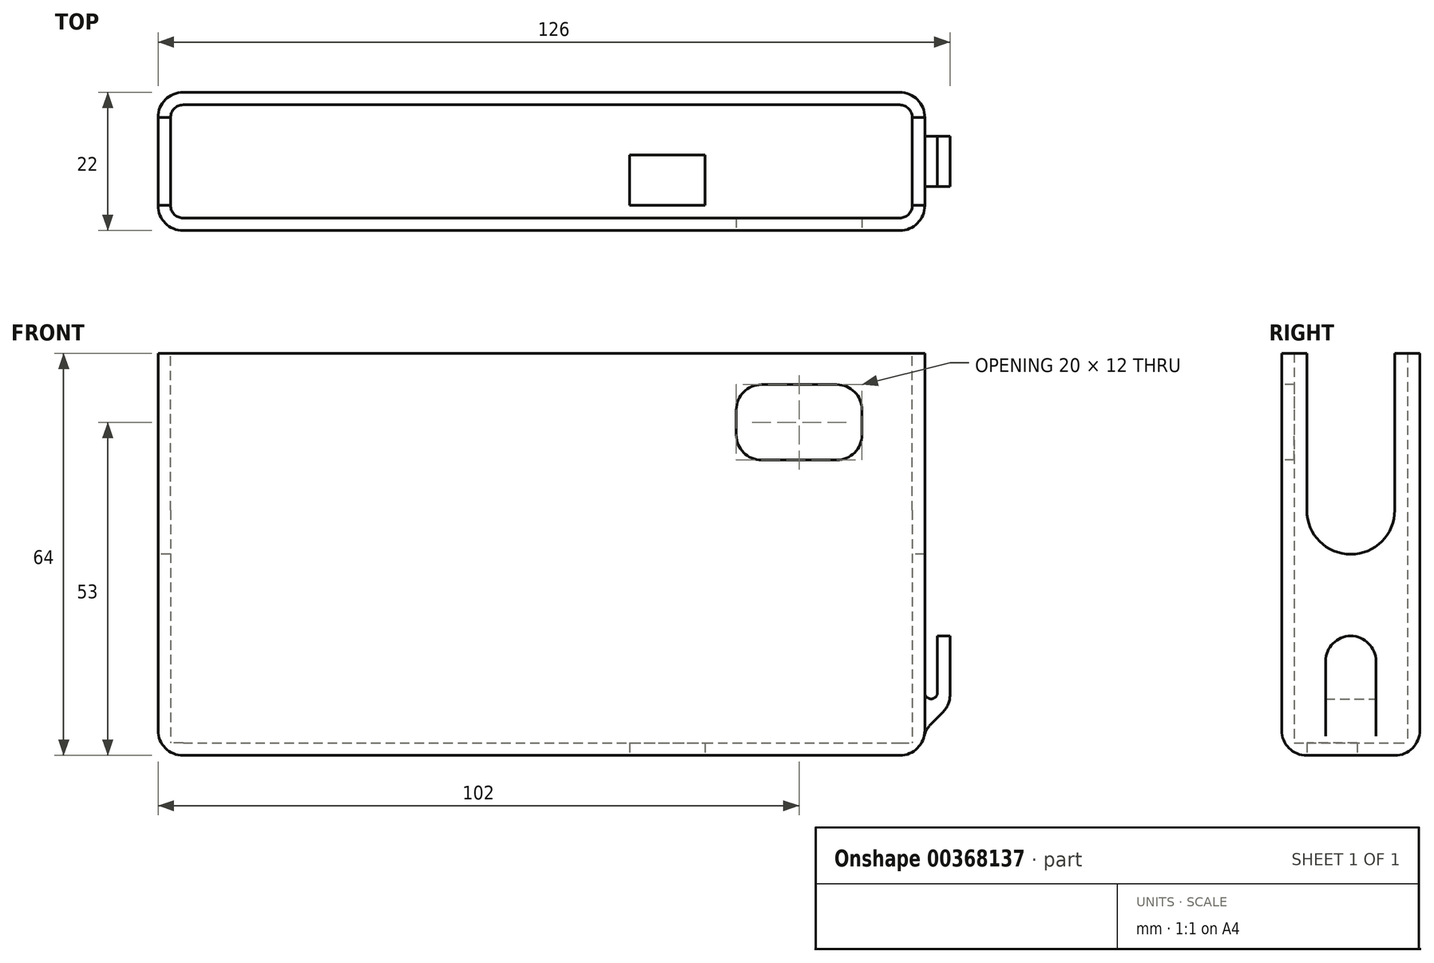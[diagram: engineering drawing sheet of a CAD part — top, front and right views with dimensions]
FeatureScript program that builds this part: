
annotation { "Feature Type Name" : "Feature", "Feature Type Description" : "" }
export const myFeature = defineFeature(function(context is Context, id is Id, definition is map)
    precondition{}
    {
        {
            var Q0;
            Q0=qCreatedBy(makeId("Top.planeOp"),FACE);
            var sketch = newSketch(context, id + "F0", { "sketchPlane" : qUnion([Q0])});
            skLineSegment(sketch, "E0.bottom", {"start": v(0, 0) * mm, "end": v(122, 0) * mm});
            skLineSegment(sketch, "E0.top", {"start": v(0, 22) * mm, "end": v(122, 22) * mm});
            skLineSegment(sketch, "E0.left", {"start": v(0, 0) * mm, "end": v(0, 22) * mm});
            skLineSegment(sketch, "E0.right", {"start": v(122, 0) * mm, "end": v(122, 22) * mm});
            skSolve(sketch);
        }
        {
            var Q0;
            Q0 = qSketchRegion(id + "F0", true);
            extrude(context, id + "F1", {"entities" : qUnion([Q0]), "depth" : 2 * mm});
        }
        {
            var Q0;
            Q0=makeQuery(id+"F1.opExtrude","CAP_FACE",FACE,{"disambiguationData":[OSD([sQuery(id+"F0.wireOp",EDGE,"E0.bottom"),sQuery(id+"F0.wireOp",EDGE,"E0.top"),sQuery(id+"F0.wireOp",EDGE,"E0.left"),sQuery(id+"F0.wireOp",EDGE,"E0.right")])],"isStart":false});
            var sketch = newSketch(context, id + "F2", { "sketchPlane" : qUnion([Q0])});
            skLineSegment(sketch, "E1.0", {"start": v(0, 22) * mm, "end": v(122, 22) * mm});
            skLineSegment(sketch, "E1.1", {"start": v(0, 0) * mm, "end": v(0, 22) * mm});
            skLineSegment(sketch, "E1.2", {"start": v(0, 0) * mm, "end": v(122, 0) * mm});
            skLineSegment(sketch, "E1.3", {"start": v(122, 0) * mm, "end": v(122, 22) * mm});
            skLineSegment(sketch, "E2.0", {"start": v(2, 20) * mm, "end": v(120, 20) * mm});
            skLineSegment(sketch, "E2.1", {"start": v(2, 2) * mm, "end": v(2, 20) * mm});
            skLineSegment(sketch, "E2.2", {"start": v(2, 2) * mm, "end": v(120, 2) * mm});
            skLineSegment(sketch, "E2.3", {"start": v(120, 2) * mm, "end": v(120, 20) * mm});
            skSolve(sketch);
        }
        {
            var Q0;
            Q0 = qSketchRegion(id + "F2", true);
            extrude(context, id + "F3", {"entities" : qUnion([Q0]), "operationType" : NewBodyOperationType.ADD, "depth" : 62 * mm});
        }
        {
            var Q0;
            Q0=makeQuery(id+"F3.opExtrude","SWEPT_EDGE",EDGE,{"disambiguationData":[OSD([sQuery(id+"F2.wireOp",EDGE,"E2.1"),sQuery(id+"F2.wireOp",EDGE,"E2.2")])]});
            var Q1;
            Q1=makeQuery(id+"F3.opExtrude","SWEPT_EDGE",EDGE,{"disambiguationData":[OSD([sQuery(id+"F2.wireOp",EDGE,"E2.0"),sQuery(id+"F2.wireOp",EDGE,"E2.1")])]});
            var Q2;
            Q2=makeQuery(id+"F3.opExtrude","SWEPT_EDGE",EDGE,{"disambiguationData":[OSD([sQuery(id+"F2.wireOp",EDGE,"E2.0"),sQuery(id+"F2.wireOp",EDGE,"E2.3")])]});
            var Q3;
            Q3=makeQuery(id+"F3.opExtrude","SWEPT_EDGE",EDGE,{"disambiguationData":[OSD([sQuery(id+"F2.wireOp",EDGE,"E2.2"),sQuery(id+"F2.wireOp",EDGE,"E2.3")])]});
            var Q4;
            Q4=makeQuery(id+"F3.opExtrude","CAP_EDGE",EDGE,{"disambiguationData":[OSD([sQuery(id+"F2.wireOp",EDGE,"E2.2")])],"isStart":true});
            var Q5;
            Q5=makeQuery(id+"F3.opExtrude","CAP_EDGE",EDGE,{"disambiguationData":[OSD([sQuery(id+"F2.wireOp",EDGE,"E2.3")])],"isStart":true});
            var Q6;
            Q6=makeQuery(id+"F3.opExtrude","CAP_EDGE",EDGE,{"disambiguationData":[OSD([sQuery(id+"F2.wireOp",EDGE,"E2.0")])],"isStart":true});
            var Q7;
            Q7=makeQuery(id+"F3.opExtrude","CAP_EDGE",EDGE,{"disambiguationData":[OSD([sQuery(id+"F2.wireOp",EDGE,"E2.1")])],"isStart":true});
            fillet(context, id + "F4", {"entities" : qUnion([Q0, Q1, Q2, Q3, Q4, Q5, Q6, Q7]), "radius" : 2 * mm, "tangentPropagation" : true, "allowEdgeOverflow" : false});
        }
        {
            var Q0;
            Q0=makeQuery(id+"F3.boolean.opBoolean","MERGE",EDGE,{"derivedFrom":[makeQuery(id+"F1.opExtrude","SWEPT_EDGE",EDGE,{"disambiguationData":[OSD([sQuery(id+"F0.wireOp",EDGE,"E0.bottom"),sQuery(id+"F0.wireOp",EDGE,"E0.left")])]}),makeQuery(id+"F3.opExtrude","SWEPT_EDGE",EDGE,{"disambiguationData":[OSD([sQuery(id+"F2.wireOp",EDGE,"E1.1"),sQuery(id+"F2.wireOp",EDGE,"E1.2")])]})]});
            var Q1;
            Q1=makeQuery(id+"F3.boolean.opBoolean","MERGE",EDGE,{"derivedFrom":[makeQuery(id+"F1.opExtrude","SWEPT_EDGE",EDGE,{"disambiguationData":[OSD([sQuery(id+"F0.wireOp",EDGE,"E0.top"),sQuery(id+"F0.wireOp",EDGE,"E0.left")])]}),makeQuery(id+"F3.opExtrude","SWEPT_EDGE",EDGE,{"disambiguationData":[OSD([sQuery(id+"F2.wireOp",EDGE,"E1.0"),sQuery(id+"F2.wireOp",EDGE,"E1.1")])]})]});
            var Q2;
            Q2=makeQuery(id+"F3.boolean.opBoolean","MERGE",EDGE,{"derivedFrom":[makeQuery(id+"F1.opExtrude","SWEPT_EDGE",EDGE,{"disambiguationData":[OSD([sQuery(id+"F0.wireOp",EDGE,"E0.top"),sQuery(id+"F0.wireOp",EDGE,"E0.right")])]}),makeQuery(id+"F3.opExtrude","SWEPT_EDGE",EDGE,{"disambiguationData":[OSD([sQuery(id+"F2.wireOp",EDGE,"E1.0"),sQuery(id+"F2.wireOp",EDGE,"E1.3")])]})]});
            var Q3;
            Q3=makeQuery(id+"F3.boolean.opBoolean","MERGE",EDGE,{"derivedFrom":[makeQuery(id+"F1.opExtrude","SWEPT_EDGE",EDGE,{"disambiguationData":[OSD([sQuery(id+"F0.wireOp",EDGE,"E0.bottom"),sQuery(id+"F0.wireOp",EDGE,"E0.right")])]}),makeQuery(id+"F3.opExtrude","SWEPT_EDGE",EDGE,{"disambiguationData":[OSD([sQuery(id+"F2.wireOp",EDGE,"E1.2"),sQuery(id+"F2.wireOp",EDGE,"E1.3")])]})]});
            var Q4;
            Q4=makeQuery(id+"F1.opExtrude","CAP_EDGE",EDGE,{"disambiguationData":[OSD([sQuery(id+"F0.wireOp",EDGE,"E0.bottom")])],"isStart":true});
            var Q5;
            Q5=makeQuery(id+"F1.opExtrude","CAP_EDGE",EDGE,{"disambiguationData":[OSD([sQuery(id+"F0.wireOp",EDGE,"E0.left")])],"isStart":true});
            var Q6;
            Q6=makeQuery(id+"F1.opExtrude","CAP_EDGE",EDGE,{"disambiguationData":[OSD([sQuery(id+"F0.wireOp",EDGE,"E0.top")])],"isStart":true});
            var Q7;
            Q7=makeQuery(id+"F1.opExtrude","CAP_EDGE",EDGE,{"disambiguationData":[OSD([sQuery(id+"F0.wireOp",EDGE,"E0.right")])],"isStart":true});
            fillet(context, id + "F5", {"entities" : qUnion([Q0, Q1, Q2, Q3, Q4, Q5, Q6, Q7]), "radius" : 4 * mm, "tangentPropagation" : true, "allowEdgeOverflow" : false});
        }
        {
            var Q0;
            Q0=makeQuery(id+"F3.boolean.opBoolean","MERGE",FACE,{"derivedFrom":[makeQuery(id+"F1.opExtrude","SWEPT_FACE",FACE,{"disambiguationData":[OSD([sQuery(id+"F0.wireOp",EDGE,"E0.left")])]}),makeQuery(id+"F3.opExtrude","SWEPT_FACE",FACE,{"disambiguationData":[OSD([sQuery(id+"F2.wireOp",EDGE,"E1.1")])]})]});
            var sketch = newSketch(context, id + "F6", { "sketchPlane" : qUnion([Q0])});
            skLineSegment(sketch, "E3", {"start": v(-11, 64) * mm, "end": v(-11, 39) * mm, "construction": true});
            skArc(sketch, "E4.0.startCap", {"start": v(-18, 64) * mm, "mid": v(-11, 71) * mm, "end": v(-4, 64) * mm});
            skArc(sketch, "E4.0.endCap", {"start": v(-4, 39) * mm, "mid": v(-11, 32) * mm, "end": v(-18, 39) * mm});
            skLineSegment(sketch, "E4.0.left", {"start": v(-4, 64) * mm, "end": v(-4, 39) * mm});
            skLineSegment(sketch, "E4.0.right", {"start": v(-18, 64) * mm, "end": v(-18, 39) * mm});
            skSolve(sketch);
        }
        {
            var Q0;
            Q0 = qSketchRegion(id + "F6", true);
            extrude(context, id + "F7", {"entities" : qUnion([Q0]), "operationType" : NewBodyOperationType.REMOVE, "endBound" : BoundingType.THROUGH_ALL, "oppositeDirection" : true, "depth" : 25 * mm});
        }
        {
            var Q0;
            Q0=makeQuery(id+"F3.boolean.opBoolean","MERGE",FACE,{"derivedFrom":[makeQuery(id+"F1.opExtrude","SWEPT_FACE",FACE,{"disambiguationData":[OSD([sQuery(id+"F0.wireOp",EDGE,"E0.bottom")])]}),makeQuery(id+"F3.opExtrude","SWEPT_FACE",FACE,{"disambiguationData":[OSD([sQuery(id+"F2.wireOp",EDGE,"E1.2")])]})]});
            var sketch = newSketch(context, id + "F8", { "sketchPlane" : qUnion([Q0])});
            skLineSegment(sketch, "E5.bottom", {"start": v(96, 59) * mm, "end": v(108, 59) * mm});
            skLineSegment(sketch, "E5.top", {"start": v(96, 47) * mm, "end": v(108, 47) * mm});
            skLineSegment(sketch, "E5.left", {"start": v(92, 55) * mm, "end": v(92, 51) * mm});
            skLineSegment(sketch, "E5.right", {"start": v(112, 55) * mm, "end": v(112, 51) * mm});
            skPoint(sketch, "E6", {"position": v(92, 53) * mm});
            skPoint(sketch, "E7.visualSharp", {"position": v(92, 59) * mm});
            skArc(sketch, "E7.filletArc", {"start": v(96, 59) * mm, "mid": v(93.17, 57.83) * mm, "end": v(92, 55) * mm});
            skPoint(sketch, "E8.visualSharp", {"position": v(112, 59) * mm});
            skArc(sketch, "E8.filletArc", {"start": v(112, 55) * mm, "mid": v(110.83, 57.83) * mm, "end": v(108, 59) * mm});
            skPoint(sketch, "E9.visualSharp", {"position": v(112, 47) * mm});
            skArc(sketch, "E9.filletArc", {"start": v(108, 47) * mm, "mid": v(110.83, 48.17) * mm, "end": v(112, 51) * mm});
            skPoint(sketch, "E10.visualSharp", {"position": v(92, 47) * mm});
            skArc(sketch, "E10.filletArc", {"start": v(92, 51) * mm, "mid": v(93.17, 48.17) * mm, "end": v(96, 47) * mm});
            skPoint(sketch, "E11", {"position": v(102, 59) * mm});
            skSolve(sketch);
        }
        {
            var Q0;
            Q0 = qSketchRegion(id + "F8", true);
            extrude(context, id + "F9", {"entities" : qUnion([Q0]), "operationType" : NewBodyOperationType.REMOVE, "endBound" : BoundingType.UP_TO_NEXT, "oppositeDirection" : true, "depth" : 25 * mm});
        }
        {
            var Q0;
            Q0=makeQuery(id+"F1.opExtrude","CAP_FACE",FACE,{"disambiguationData":[OSD([sQuery(id+"F0.wireOp",EDGE,"E0.bottom"),sQuery(id+"F0.wireOp",EDGE,"E0.top"),sQuery(id+"F0.wireOp",EDGE,"E0.left"),sQuery(id+"F0.wireOp",EDGE,"E0.right")])],"isStart":true});
            var sketch = newSketch(context, id + "F10", { "sketchPlane" : qUnion([Q0])});
            skLineSegment(sketch, "E12.bottom", {"start": v(75, -4) * mm, "end": v(87, -4) * mm});
            skLineSegment(sketch, "E12.top", {"start": v(75, -12) * mm, "end": v(87, -12) * mm});
            skLineSegment(sketch, "E12.left", {"start": v(75, -4) * mm, "end": v(75, -12) * mm});
            skLineSegment(sketch, "E12.right", {"start": v(87, -4) * mm, "end": v(87, -12) * mm});
            skPoint(sketch, "E13", {"position": v(81, -4) * mm});
            skPoint(sketch, "E14", {"position": v(87, -8) * mm});
            skSolve(sketch);
        }
        {
            var Q0;
            Q0 = qSketchRegion(id + "F10", true);
            extrude(context, id + "F11", {"entities" : qUnion([Q0]), "operationType" : NewBodyOperationType.REMOVE, "endBound" : BoundingType.THROUGH_ALL, "oppositeDirection" : true, "depth" : 25 * mm});
        }
        {
            var Q0;
            Q0=makeQuery(id+"F3.boolean.opBoolean","MERGE",FACE,{"derivedFrom":[makeQuery(id+"F1.opExtrude","SWEPT_FACE",FACE,{"disambiguationData":[OSD([sQuery(id+"F0.wireOp",EDGE,"E0.right")])]}),makeQuery(id+"F3.opExtrude","SWEPT_FACE",FACE,{"disambiguationData":[OSD([sQuery(id+"F2.wireOp",EDGE,"E1.3")])]})]});
            var sketch = newSketch(context, id + "F12", { "sketchPlane" : qUnion([Q0])});
            skLineSegment(sketch, "E15.bottom", {"start": v(7, 19) * mm, "end": v(15, 19) * mm});
            skLineSegment(sketch, "E15.top", {"start": v(7, 4) * mm, "end": v(15, 4) * mm});
            skLineSegment(sketch, "E15.left", {"start": v(7, 19) * mm, "end": v(7, 4) * mm});
            skLineSegment(sketch, "E15.right", {"start": v(15, 19) * mm, "end": v(15, 4) * mm});
            skPoint(sketch, "E16", {"position": v(11, 4) * mm});
            skSolve(sketch);
        }
        {
            var Q0;
            Q0 = qSketchRegion(id + "F12", true);
            extrude(context, id + "F13", {"entities" : qUnion([Q0]), "operationType" : NewBodyOperationType.ADD, "depth" : 4 * mm});
        }
        {
            var Q0;
            Q0=makeQuery(id+"F13.opExtrude","CAP_EDGE",EDGE,{"disambiguationData":[OSD([sQuery(id+"F12.wireOp",EDGE,"E15.top")])],"isStart":false});
            chamfer(context, id + "F14", {"entities" : qUnion([Q0]), "width" : 4 * mm, "tangentPropagation" : true});
        }
        {
            var Q0;
            Q0=makeQuery(id+"F13.opExtrude","SWEPT_FACE",FACE,{"disambiguationData":[OSD([sQuery(id+"F12.wireOp",EDGE,"E15.bottom")])]});
            var sketch = newSketch(context, id + "F15", { "sketchPlane" : qUnion([Q0])});
            skLineSegment(sketch, "E17.bottom", {"start": v(122, 7) * mm, "end": v(124, 7) * mm});
            skLineSegment(sketch, "E17.top", {"start": v(122, 15) * mm, "end": v(124, 15) * mm});
            skLineSegment(sketch, "E17.left", {"start": v(122, 7) * mm, "end": v(122, 15) * mm});
            skLineSegment(sketch, "E17.right", {"start": v(124, 7) * mm, "end": v(124, 15) * mm});
            skSolve(sketch);
        }
        {
            var Q0;
            Q0 = qSketchRegion(id + "F15", true);
            extrude(context, id + "F16", {"entities" : qUnion([Q0]), "operationType" : NewBodyOperationType.REMOVE, "oppositeDirection" : true, "depth" : 10 * mm});
        }
        {
            var Q0;
            Q0=makeQuery(id+"F13.opExtrude","SWEPT_EDGE",EDGE,{"disambiguationData":[OSD([sQuery(id+"F12.wireOp",EDGE,"E15.bottom"),sQuery(id+"F12.wireOp",EDGE,"E15.left")])]});
            var Q1;
            Q1=makeQuery(id+"F13.opExtrude","SWEPT_EDGE",EDGE,{"disambiguationData":[OSD([sQuery(id+"F12.wireOp",EDGE,"E15.bottom"),sQuery(id+"F12.wireOp",EDGE,"E15.right")])]});
            var Q2;
            {var subQ0=sQuery(id+"F12.wireOp",EDGE,"E15.top");Q2=makeQuery(id+"F14.opChamfer","BLEND_EDGE",EDGE,{"blendedFrom":[makeQuery(id+"F13.opExtrude","CAP_EDGE",EDGE,{"disambiguationData":[OSD([subQ0])],"isStart":false}),makeQuery(id+"F13.opExtrude","CAP_FACE",FACE,{"disambiguationData":[OSD([sQuery(id+"F12.wireOp",EDGE,"E15.bottom"),subQ0,sQuery(id+"F12.wireOp",EDGE,"E15.left"),sQuery(id+"F12.wireOp",EDGE,"E15.right")])],"isStart":false})],"blendedInto":[makeQuery(id+"F13.opExtrude","CAP_FACE",FACE,{"disambiguationData":[OSD([sQuery(id+"F12.wireOp",EDGE,"E15.bottom"),subQ0,sQuery(id+"F12.wireOp",EDGE,"E15.left"),sQuery(id+"F12.wireOp",EDGE,"E15.right")])],"isStart":false})]});}
            var Q3;
            Q3=makeQuery(id+"F14.opChamfer","BLEND_EDGE",EDGE,{"blendedFrom":[makeQuery(id+"F13.opExtrude","CAP_EDGE",EDGE,{"disambiguationData":[OSD([sQuery(id+"F12.wireOp",EDGE,"E15.top")])],"isStart":false}),makeQuery(id+"F5.opFillet","BLEND_FACE",FACE,{"disambiguationData":[OSD([sQuery(id+"F0.wireOp",EDGE,"E0.right")])]})],"blendedInto":[makeQuery(id+"F5.opFillet","BLEND_FACE",FACE,{"disambiguationData":[OSD([sQuery(id+"F0.wireOp",EDGE,"E0.right")])]})]});
            fillet(context, id + "F17", {"entities" : qUnion([Q0, Q1, Q2, Q3]), "radius" : 4 * mm, "tangentPropagation" : true, "allowEdgeOverflow" : false});
        }
        {
            var Q0;
            Q0=makeQuery(id+"F16.boolean.opBoolean","COPY",EDGE,{"derivedFrom":makeQuery(id+"F16.opExtrude","CAP_EDGE",EDGE,{"disambiguationData":[OSD([sQuery(id+"F15.wireOp",EDGE,"E17.right")])],"isStart":false})});
            var Q1;
            Q1=makeQuery(id+"F16.boolean.opBoolean","COPY",EDGE,{"derivedFrom":makeQuery(id+"F16.opExtrude","CAP_EDGE",EDGE,{"disambiguationData":[OSD([sQuery(id+"F15.wireOp",EDGE,"E17.left")])],"isStart":false})});
            fillet(context, id + "F18", {"entities" : qUnion([Q0, Q1]), "radius" : 1 * mm, "tangentPropagation" : true, "allowEdgeOverflow" : false});
        }
    });
